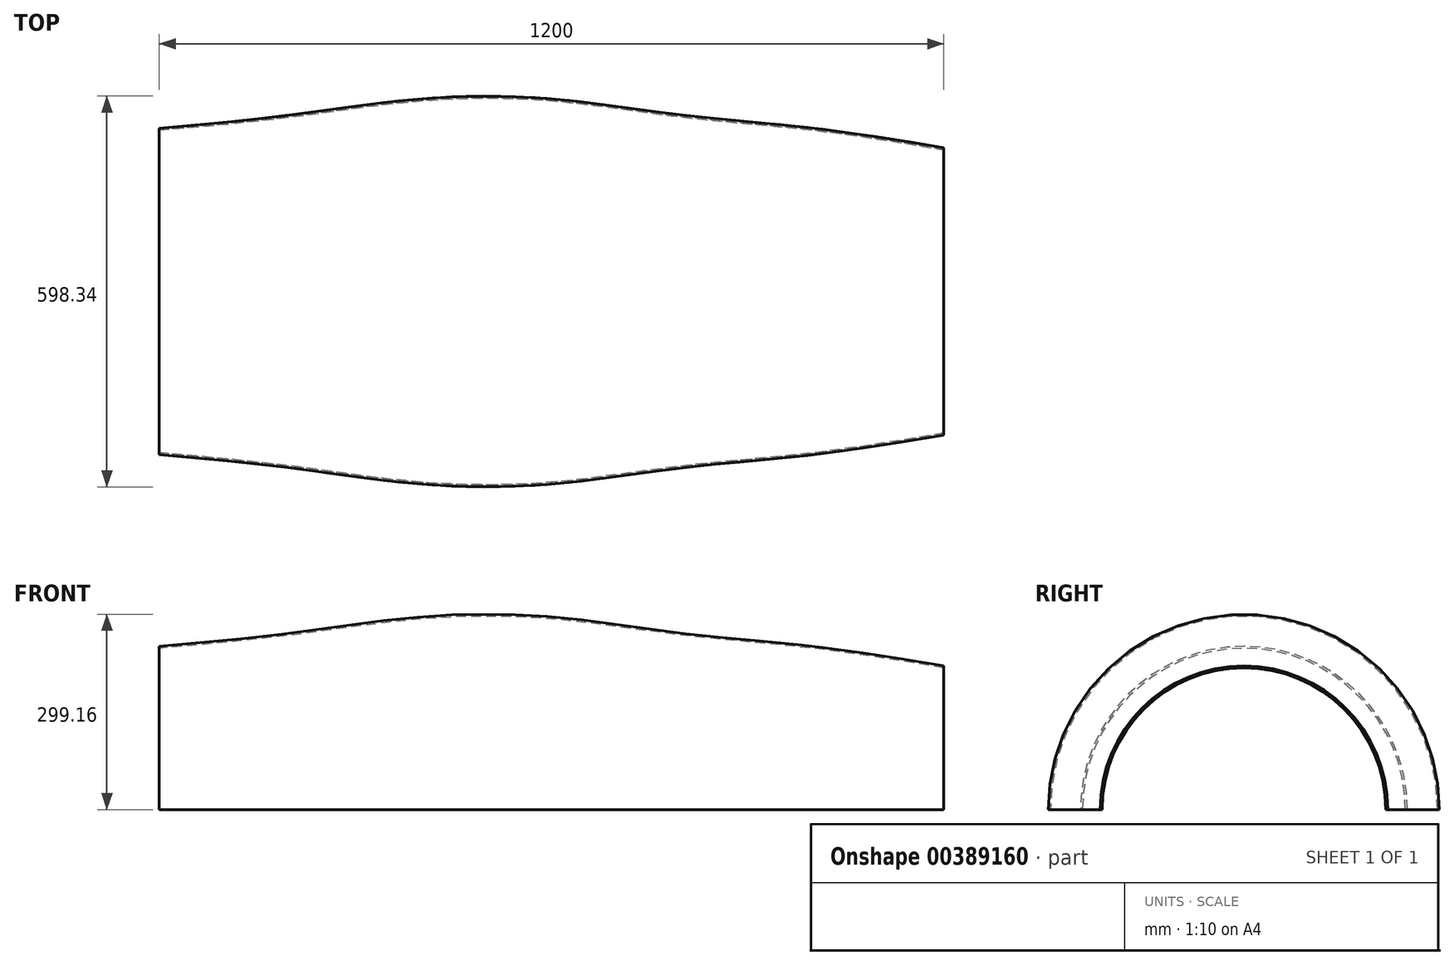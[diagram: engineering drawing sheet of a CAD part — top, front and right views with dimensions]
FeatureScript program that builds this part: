
annotation { "Feature Type Name" : "Feature", "Feature Type Description" : "" }
export const myFeature = defineFeature(function(context is Context, id is Id, definition is map)
    precondition{}
    {
        {
            var Q0;
            Q0=qCreatedBy(makeId("Right.planeOp"),FACE);
            cPlane(context, id + "F0", {"entities" : qUnion([Q0]), "cplaneType" : CPlaneType.OFFSET, "offset" : 200 * mm, "width" : 150 * mm, "height" : 150 * mm});
        }
        {
            var Q0;
            Q0=qCreatedBy(makeId("Right.planeOp"),FACE);
            cPlane(context, id + "F1", {"entities" : qUnion([Q0]), "cplaneType" : CPlaneType.OFFSET, "offset" : 400 * mm, "width" : 150 * mm, "height" : 150 * mm});
        }
        {
            var Q0;
            Q0=qCreatedBy(id+"F1.planeOp",FACE);
            cPlane(context, id + "F2", {"entities" : qUnion([Q0]), "cplaneType" : CPlaneType.OFFSET, "offset" : 200 * mm, "width" : 150 * mm, "height" : 150 * mm});
        }
        {
            var Q0;
            Q0=qCreatedBy(id+"F2.planeOp",FACE);
            cPlane(context, id + "F3", {"entities" : qUnion([Q0]), "cplaneType" : CPlaneType.OFFSET, "offset" : 200 * mm, "width" : 150 * mm, "height" : 150 * mm});
        }
        {
            var Q0;
            Q0=qCreatedBy(id+"F3.planeOp",FACE);
            cPlane(context, id + "F4", {"entities" : qUnion([Q0]), "cplaneType" : CPlaneType.OFFSET, "offset" : 200 * mm, "width" : 150 * mm, "height" : 150 * mm});
        }
        {
            var Q0;
            Q0=qCreatedBy(id+"F4.planeOp",FACE);
            cPlane(context, id + "F5", {"entities" : qUnion([Q0]), "cplaneType" : CPlaneType.OFFSET, "offset" : 200 * mm, "width" : 150 * mm, "height" : 150 * mm});
        }
        {
            var Q0;
            Q0=qCreatedBy(makeId("Right.planeOp"),FACE);
            var sketch = newSketch(context, id + "F6", { "sketchPlane" : qUnion([Q0])});
            skArc(sketch, "E0", {"start": v(250, 0) * mm, "mid": v(0, 250) * mm, "end": v(-250, 0) * mm});
            skArc(sketch, "E1.0", {"start": v(247, 0) * mm, "mid": v(0, 247) * mm, "end": v(-247, 0) * mm});
            skLineSegment(sketch, "E2", {"start": v(-250, 0) * mm, "end": v(-247, 0) * mm});
            skLineSegment(sketch, "E3", {"start": v(247, 0) * mm, "end": v(250, 0) * mm});
            skSolve(sketch);
        }
        {
            var Q0;
            Q0=qCreatedBy(id+"F0.planeOp",FACE);
            var sketch = newSketch(context, id + "F7", { "sketchPlane" : qUnion([Q0])});
            skArc(sketch, "E4", {"start": v(270, 0) * mm, "mid": v(0, 270) * mm, "end": v(-270, 0) * mm});
            skArc(sketch, "E5.0", {"start": v(267, 0) * mm, "mid": v(0, 267) * mm, "end": v(-267, 0) * mm});
            skLineSegment(sketch, "E6", {"start": v(-267, 0) * mm, "end": v(-270, 0) * mm});
            skLineSegment(sketch, "E7", {"start": v(267, 0) * mm, "end": v(270, 0) * mm});
            skSolve(sketch);
        }
        {
            var Q0;
            Q0=qCreatedBy(id+"F1.planeOp",FACE);
            var sketch = newSketch(context, id + "F8", { "sketchPlane" : qUnion([Q0])});
            skArc(sketch, "E8", {"start": v(295, 0) * mm, "mid": v(0, 295) * mm, "end": v(-295, 0) * mm});
            skArc(sketch, "E9.0", {"start": v(292, 0) * mm, "mid": v(0, 292) * mm, "end": v(-292, 0) * mm});
            skLineSegment(sketch, "E10", {"start": v(-295, 0) * mm, "end": v(-292, 0) * mm});
            skLineSegment(sketch, "E11", {"start": v(292, 0) * mm, "end": v(295, 0) * mm});
            skSolve(sketch);
        }
        {
            var Q0;
            Q0=qCreatedBy(id+"F2.planeOp",FACE);
            var sketch = newSketch(context, id + "F9", { "sketchPlane" : qUnion([Q0])});
            skArc(sketch, "E12", {"start": v(295, 0) * mm, "mid": v(0, 295) * mm, "end": v(-295, 0) * mm});
            skArc(sketch, "E13.0", {"start": v(292, 0) * mm, "mid": v(0, 292) * mm, "end": v(-292, 0) * mm});
            skLineSegment(sketch, "E14", {"start": v(-295, 0) * mm, "end": v(-292, 0) * mm});
            skLineSegment(sketch, "E15", {"start": v(292, 0) * mm, "end": v(295, 0) * mm});
            skSolve(sketch);
        }
        {
            var Q0;
            Q0=qCreatedBy(id+"F3.planeOp",FACE);
            var sketch = newSketch(context, id + "F10", { "sketchPlane" : qUnion([Q0])});
            skArc(sketch, "E16", {"start": v(270, 0) * mm, "mid": v(0, 270) * mm, "end": v(-270, 0) * mm});
            skArc(sketch, "E17.0", {"start": v(267, 0) * mm, "mid": v(0, 267) * mm, "end": v(-267, 0) * mm});
            skLineSegment(sketch, "E18", {"start": v(-270, 0) * mm, "end": v(-267, 0) * mm});
            skLineSegment(sketch, "E19", {"start": v(267, 0) * mm, "end": v(270, 0) * mm});
            skSolve(sketch);
        }
        {
            var Q0;
            Q0=qCreatedBy(id+"F4.planeOp",FACE);
            var sketch = newSketch(context, id + "F11", { "sketchPlane" : qUnion([Q0])});
            skArc(sketch, "E20", {"start": v(250, 0) * mm, "mid": v(0, 250) * mm, "end": v(-250, 0) * mm});
            skArc(sketch, "E21.0", {"start": v(247, 0) * mm, "mid": v(0, 247) * mm, "end": v(-247, 0) * mm});
            skLineSegment(sketch, "E22", {"start": v(-250, 0) * mm, "end": v(-247, 0) * mm});
            skLineSegment(sketch, "E23", {"start": v(247, 0) * mm, "end": v(250, 0) * mm});
            skSolve(sketch);
        }
        {
            var Q0;
            Q0=qCreatedBy(id+"F5.planeOp",FACE);
            var sketch = newSketch(context, id + "F12", { "sketchPlane" : qUnion([Q0])});
            skArc(sketch, "E24", {"start": v(220, 0) * mm, "mid": v(0, 220) * mm, "end": v(-220, 0) * mm});
            skArc(sketch, "E25.0", {"start": v(217, 0) * mm, "mid": v(0, 217) * mm, "end": v(-217, 0) * mm});
            skLineSegment(sketch, "E26", {"start": v(-220, 0) * mm, "end": v(-217, 0) * mm});
            skLineSegment(sketch, "E27", {"start": v(217, 0) * mm, "end": v(220, 0) * mm});
            skSolve(sketch);
        }
        {
            var Q0;
            Q0=makeQuery(id+"F6.imprint","IMPRINT",FACE,{"disambiguationData":[TD([[makeQuery(id+"F6.imprint","IMPRINT",EDGE,{"derivedFrom":sQuery(id+"F6.wireOp",EDGE,"E0")}),1.0]])]});
            var Q1;
            Q1=makeQuery(id+"F7.imprint","IMPRINT",FACE,{"disambiguationData":[TD([[makeQuery(id+"F7.imprint","IMPRINT",EDGE,{"derivedFrom":sQuery(id+"F7.wireOp",EDGE,"E4")}),1.0]])]});
            var Q2;
            Q2=makeQuery(id+"F8.imprint","IMPRINT",FACE,{"disambiguationData":[TD([[makeQuery(id+"F8.imprint","IMPRINT",EDGE,{"derivedFrom":sQuery(id+"F8.wireOp",EDGE,"E8")}),1.0]])]});
            var Q3;
            Q3=makeQuery(id+"F9.imprint","IMPRINT",FACE,{"disambiguationData":[TD([[makeQuery(id+"F9.imprint","IMPRINT",EDGE,{"derivedFrom":sQuery(id+"F9.wireOp",EDGE,"E12")}),1.0]])]});
            var Q4;
            Q4=makeQuery(id+"F10.imprint","IMPRINT",FACE,{"disambiguationData":[TD([[makeQuery(id+"F10.imprint","IMPRINT",EDGE,{"derivedFrom":sQuery(id+"F10.wireOp",EDGE,"E16")}),1.0]])]});
            var Q5;
            Q5=makeQuery(id+"F11.imprint","IMPRINT",FACE,{"disambiguationData":[TD([[makeQuery(id+"F11.imprint","IMPRINT",EDGE,{"derivedFrom":sQuery(id+"F11.wireOp",EDGE,"E20")}),1.0]])]});
            var Q6;
            Q6=makeQuery(id+"F12.imprint","IMPRINT",FACE,{"disambiguationData":[TD([[makeQuery(id+"F12.imprint","IMPRINT",EDGE,{"derivedFrom":sQuery(id+"F12.wireOp",EDGE,"E24")}),1.0]])]});
            loft(context, id + "F13", {"sheetProfilesArray" : [{ "sheetProfileEntities" : qUnion([Q0]) }, { "sheetProfileEntities" : qUnion([Q1]) }, { "sheetProfileEntities" : qUnion([Q2]) }, { "sheetProfileEntities" : qUnion([Q3]) }, { "sheetProfileEntities" : qUnion([Q4]) }, { "sheetProfileEntities" : qUnion([Q5]) }, { "sheetProfileEntities" : qUnion([Q6]) }]});
        }
        {
            var Q0;
            Q0=qCreatedBy(id+"F5.planeOp",FACE);
            cPlane(context, id + "F14", {"entities" : qUnion([Q0]), "cplaneType" : CPlaneType.OFFSET, "offset" : 100 * mm, "width" : 150 * mm, "height" : 150 * mm});
        }
        {
            var Q0;
            Q0=qCreatedBy(id+"F14.planeOp",FACE);
            cPlane(context, id + "F15", {"entities" : qUnion([Q0]), "cplaneType" : CPlaneType.OFFSET, "offset" : 300 * mm, "width" : 150 * mm, "height" : 150 * mm});
        }
        {
            var Q0;
            Q0=qCreatedBy(id+"F15.planeOp",FACE);
            cPlane(context, id + "F16", {"entities" : qUnion([Q0]), "cplaneType" : CPlaneType.OFFSET, "offset" : 200 * mm, "width" : 150 * mm, "height" : 150 * mm});
        }
    });
